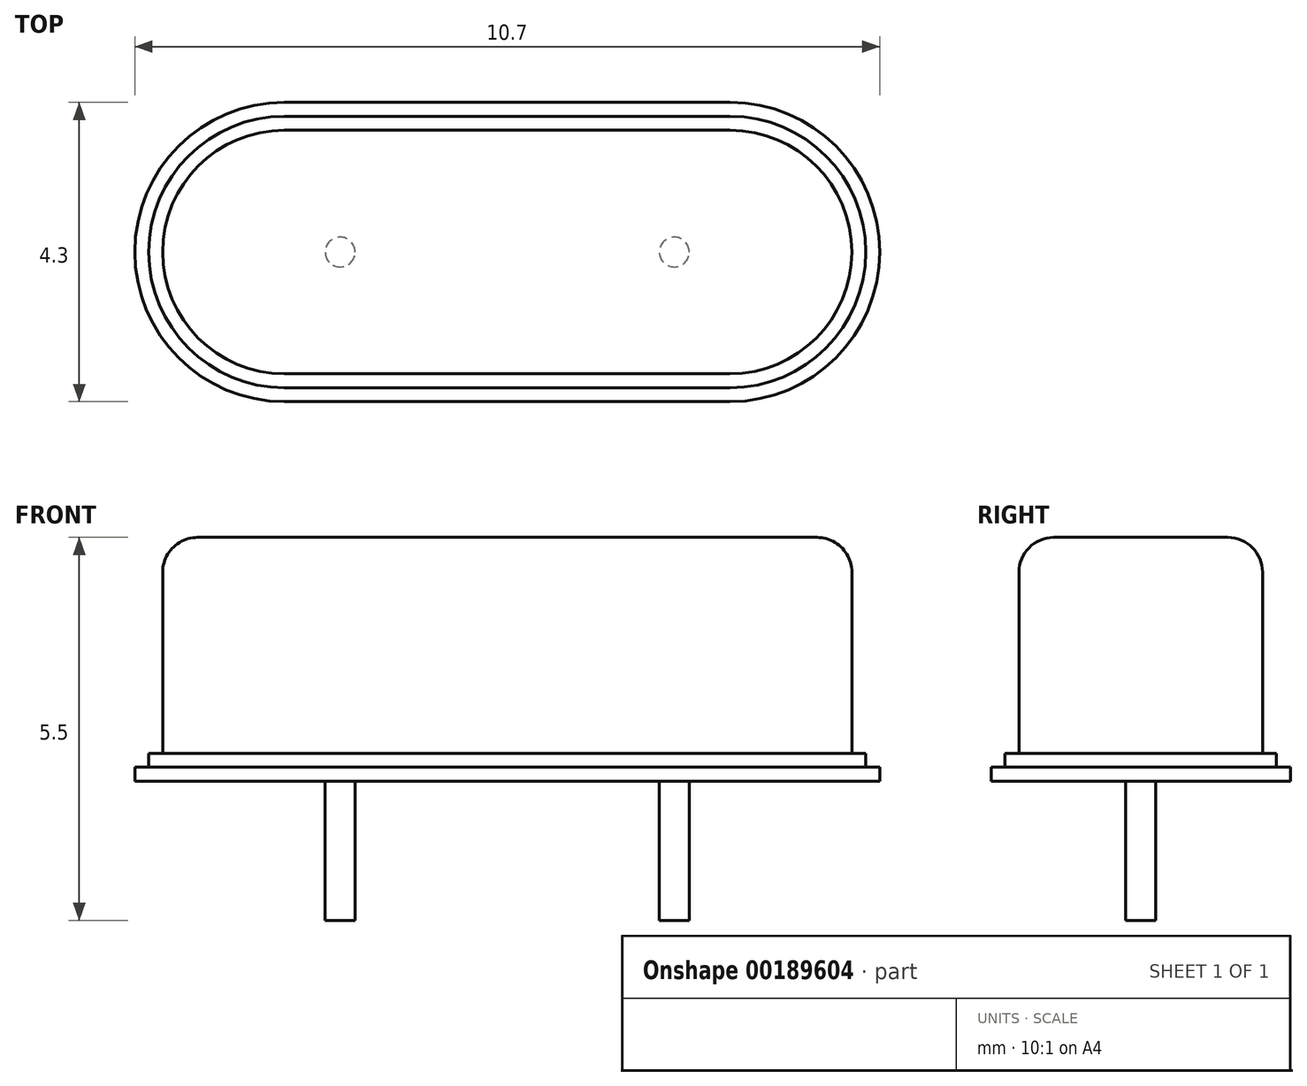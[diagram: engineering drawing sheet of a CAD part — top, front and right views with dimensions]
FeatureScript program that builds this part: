
annotation { "Feature Type Name" : "Feature", "Feature Type Description" : "" }
export const myFeature = defineFeature(function(context is Context, id is Id, definition is map)
    precondition{}
    {
        {
            var Q0;
            Q0=qCreatedBy(makeId("Top.planeOp"),FACE);
            var sketch = newSketch(context, id + "F0", { "sketchPlane" : qUnion([Q0])});
            skLineSegment(sketch, "E0.bottom", {"start": v(0, 0) * mm, "end": v(5.35, 0) * mm});
            skLineSegment(sketch, "E0.top", {"start": v(0, 2.15) * mm, "end": v(3.2, 2.15) * mm});
            skLineSegment(sketch, "E0.left", {"start": v(0, 0) * mm, "end": v(0, 2.15) * mm});
            skArc(sketch, "E1", {"start": v(5.35, 0) * mm, "mid": v(4.72, 1.52) * mm, "end": v(3.2, 2.15) * mm});
            skSolve(sketch);
        }
        {
            var Q0;
            Q0=qSketchRegion(id+"F0",true);
            extrude(context, id + "F1", {"entities" : qUnion([Q0]), "depth" : 0.2 * mm});
        }
        {
            var Q0;
            Q0=makeQuery(id+"F1.opExtrude","CAP_FACE",FACE,{"disambiguationData":[OSD([sQuery(id+"F0.wireOp",EDGE,"E0.bottom"),sQuery(id+"F0.wireOp",EDGE,"E0.top"),sQuery(id+"F0.wireOp",EDGE,"E0.left"),sQuery(id+"F0.wireOp",EDGE,"E1")])],"isStart":false});
            var sketch = newSketch(context, id + "F2", { "sketchPlane" : qUnion([Q0])});
            skArc(sketch, "E2.0", {"start": v(5.15, 0) * mm, "mid": v(4.58, 1.38) * mm, "end": v(3.2, 1.95) * mm});
            skLineSegment(sketch, "E2.1", {"start": v(0, 1.95) * mm, "end": v(3.2, 1.95) * mm});
            skLineSegment(sketch, "E3", {"start": v(0, 1.95) * mm, "end": v(0, 0) * mm});
            skLineSegment(sketch, "E4", {"start": v(0, 0) * mm, "end": v(5.15, 0) * mm});
            skSolve(sketch);
        }
        {
            var Q0;
            Q0=qSketchRegion(id+"F2",true);
            extrude(context, id + "F3", {"entities" : qUnion([Q0]), "operationType" : NewBodyOperationType.ADD, "depth" : 0.2 * mm});
        }
        {
            var Q0;
            Q0=makeQuery(id+"F3.opExtrude","CAP_FACE",FACE,{"disambiguationData":[OSD([sQuery(id+"F2.wireOp",EDGE,"E2.0"),sQuery(id+"F2.wireOp",EDGE,"E2.1"),sQuery(id+"F2.wireOp",EDGE,"E3"),sQuery(id+"F2.wireOp",EDGE,"E4")])],"isStart":false});
            var sketch = newSketch(context, id + "F4", { "sketchPlane" : qUnion([Q0])});
            skArc(sketch, "E5.0", {"start": v(4.95, 0) * mm, "mid": v(4.44, 1.24) * mm, "end": v(3.2, 1.75) * mm});
            skLineSegment(sketch, "E5.1", {"start": v(0, 1.75) * mm, "end": v(3.2, 1.75) * mm});
            skLineSegment(sketch, "E6", {"start": v(0, 1.75) * mm, "end": v(0, 0) * mm});
            skLineSegment(sketch, "E7", {"start": v(0, 0) * mm, "end": v(4.95, 0) * mm});
            skSolve(sketch);
        }
        {
            var Q0;
            Q0=qSketchRegion(id+"F4",true);
            extrude(context, id + "F5", {"entities" : qUnion([Q0]), "operationType" : NewBodyOperationType.ADD, "depth" : 3.1 * mm});
        }
        {
            var Q0;
            Q0=makeQuery(id+"F1.opExtrude","SWEPT_BODY",BODY,{"disambiguationData":[OSD([sQuery(id+"F0.wireOp",EDGE,"E0.bottom"),sQuery(id+"F0.wireOp",EDGE,"E0.top"),sQuery(id+"F0.wireOp",EDGE,"E0.left"),sQuery(id+"F0.wireOp",EDGE,"E1")])]});
            var Q1;
            Q1=makeQuery(id+"F5.boolean.opBoolean","MERGE",FACE,{"derivedFrom":[makeQuery(id+"F3.boolean.opBoolean","MERGE",FACE,{"derivedFrom":[makeQuery(id+"F1.opExtrude","SWEPT_FACE",FACE,{"disambiguationData":[OSD([sQuery(id+"F0.wireOp",EDGE,"E0.left")])]}),makeQuery(id+"F3.opExtrude","SWEPT_FACE",FACE,{"disambiguationData":[OSD([sQuery(id+"F2.wireOp",EDGE,"E3")])]})]}),makeQuery(id+"F5.opExtrude","SWEPT_FACE",FACE,{"disambiguationData":[OSD([sQuery(id+"F4.wireOp",EDGE,"E6")])]})]});
            mirror(context, id + "F6", {"operationType" : NewBodyOperationType.ADD, "entities" : qUnion([Q0]), "mirrorPlane" : qUnion([Q1])});
        }
        {
            var Q0;
            Q0=makeQuery(id+"F1.opExtrude","SWEPT_BODY",BODY,{"disambiguationData":[OSD([sQuery(id+"F0.wireOp",EDGE,"E0.bottom"),sQuery(id+"F0.wireOp",EDGE,"E0.top"),sQuery(id+"F0.wireOp",EDGE,"E0.left"),sQuery(id+"F0.wireOp",EDGE,"E1")])]});
            var Q1;
            {var subQ0=makeQuery(id+"F5.boolean.opBoolean","MERGE",FACE,{"derivedFrom":[makeQuery(id+"F3.boolean.opBoolean","MERGE",FACE,{"derivedFrom":[makeQuery(id+"F1.opExtrude","SWEPT_FACE",FACE,{"disambiguationData":[OSD([sQuery(id+"F0.wireOp",EDGE,"E0.bottom")])]}),makeQuery(id+"F3.opExtrude","SWEPT_FACE",FACE,{"disambiguationData":[OSD([sQuery(id+"F2.wireOp",EDGE,"E4")])]})]}),makeQuery(id+"F5.opExtrude","SWEPT_FACE",FACE,{"disambiguationData":[OSD([sQuery(id+"F4.wireOp",EDGE,"E7")])]})]});Q1=makeQuery(id+"F6.boolean.opBoolean","MERGE",FACE,{"derivedFrom":[subQ0,makeQuery(id+"F6.opPattern","COPY",FACE,{"derivedFrom":subQ0,"instanceName":"1"})]});}
            mirror(context, id + "F7", {"operationType" : NewBodyOperationType.ADD, "entities" : qUnion([Q0]), "mirrorPlane" : qUnion([Q1])});
        }
        {
            var Q0;
            {var subQ0=makeQuery(id+"F5.opExtrude","CAP_FACE",FACE,{"disambiguationData":[OSD([sQuery(id+"F4.wireOp",EDGE,"E5.0"),sQuery(id+"F4.wireOp",EDGE,"E5.1"),sQuery(id+"F4.wireOp",EDGE,"E6"),sQuery(id+"F4.wireOp",EDGE,"E7")])],"isStart":false});var subQ1=makeQuery(id+"F6.boolean.opBoolean","MERGE",FACE,{"derivedFrom":[subQ0,makeQuery(id+"F6.opPattern","COPY",FACE,{"derivedFrom":subQ0,"instanceName":"1"})]});Q0=makeQuery(id+"F7.boolean.opBoolean","MERGE",FACE,{"derivedFrom":[subQ1,makeQuery(id+"F7.opPattern","COPY",FACE,{"derivedFrom":subQ1,"instanceName":"1"})]});}
            fillet(context, id + "F8", {"entities" : qUnion([Q0]), "radius" : 0.5 * mm, "tangentPropagation" : true, "allowEdgeOverflow" : false});
        }
        {
            var Q0;
            {var subQ0=makeQuery(id+"F1.opExtrude","CAP_FACE",FACE,{"disambiguationData":[OSD([sQuery(id+"F0.wireOp",EDGE,"E0.bottom"),sQuery(id+"F0.wireOp",EDGE,"E0.top"),sQuery(id+"F0.wireOp",EDGE,"E0.left"),sQuery(id+"F0.wireOp",EDGE,"E1")])],"isStart":true});var subQ1=makeQuery(id+"F6.boolean.opBoolean","MERGE",FACE,{"derivedFrom":[subQ0,makeQuery(id+"F6.opPattern","COPY",FACE,{"derivedFrom":subQ0,"instanceName":"1"})]});Q0=makeQuery(id+"F7.boolean.opBoolean","MERGE",FACE,{"derivedFrom":[subQ1,makeQuery(id+"F7.opPattern","COPY",FACE,{"derivedFrom":subQ1,"instanceName":"1"})]});}
            var sketch = newSketch(context, id + "F9", { "sketchPlane" : qUnion([Q0])});
            skCircle(sketch, "E8", {"center": v(2.4, 0) * mm, "radius": 0.21 * mm});
            skLineSegment(sketch, "E9", {"start": v(0, 2.74) * mm, "end": v(0, 0.89) * mm, "construction": true});
            skCircle(sketch, "E10.0.MirrorC", {"center": v(-2.4, 0) * mm, "radius": 0.21 * mm});
            skSolve(sketch);
        }
        {
            var Q0;
            Q0=qSketchRegion(id+"F9",true);
            extrude(context, id + "F10", {"entities" : qUnion([Q0]), "operationType" : NewBodyOperationType.ADD, "depth" : 2 * mm});
        }
    });
